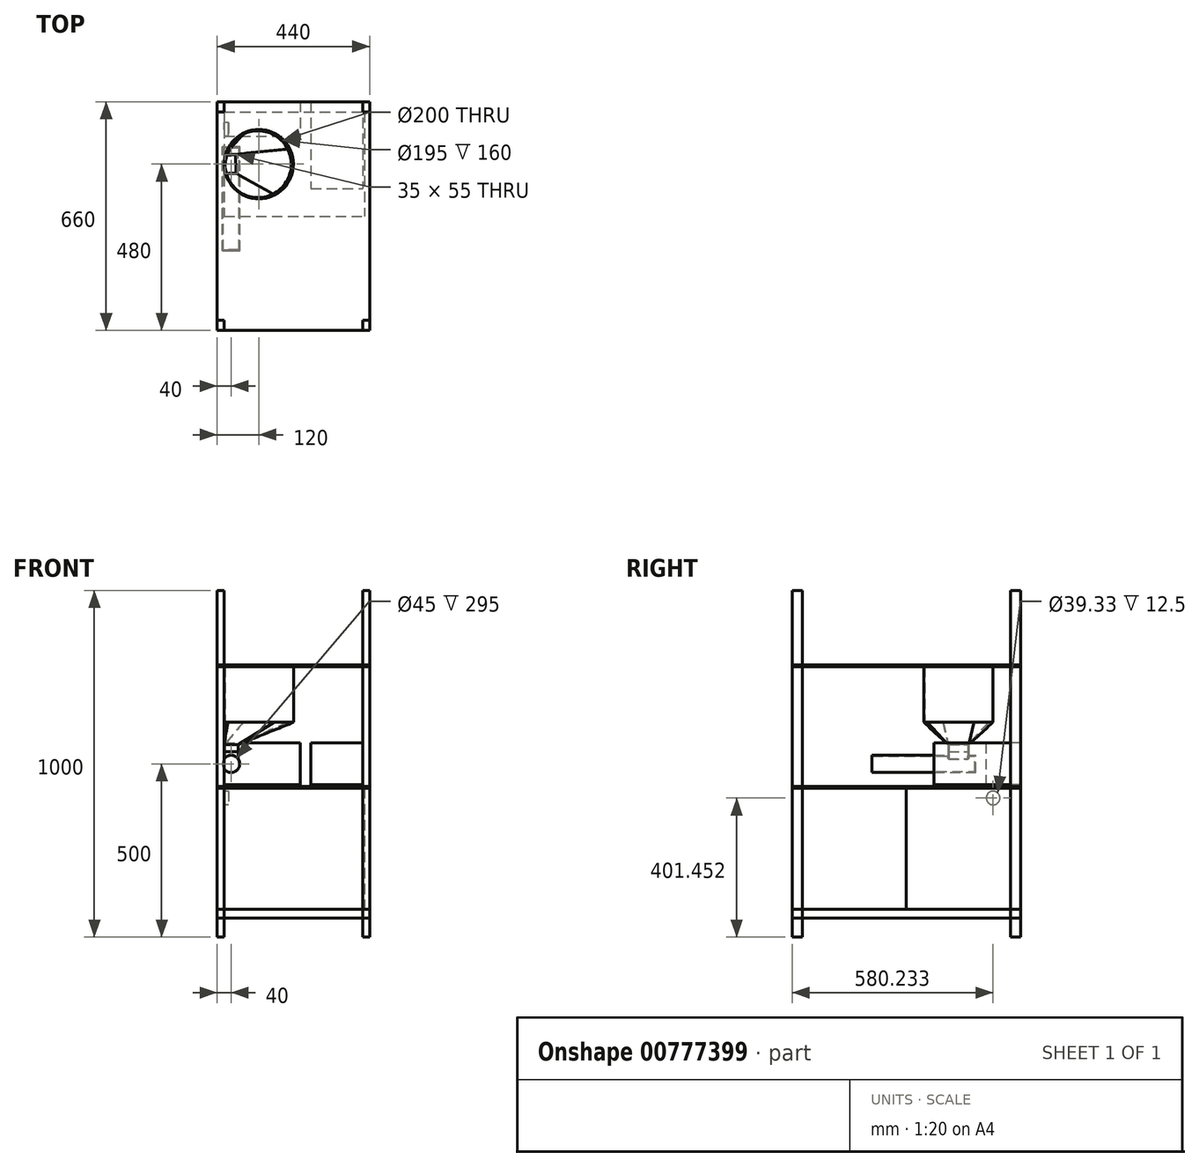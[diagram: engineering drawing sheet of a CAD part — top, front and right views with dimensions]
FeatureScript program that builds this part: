
annotation { "Feature Type Name" : "Feature", "Feature Type Description" : "" }
export const myFeature = defineFeature(function(context is Context, id is Id, definition is map)
    precondition{}
    {
        {
            var Q0;
            Q0=qCreatedBy(makeId("Front.planeOp"),FACE);
            var sketch = newSketch(context, id + "F0", { "sketchPlane" : qUnion([Q0])});
            skCircle(sketch, "E0", {"center": v(0, 0) * mm, "radius": 25 * mm});
            skSolve(sketch);
        }
        {
            var Q0;
            Q0=qSketchRegion(id+"F0",true);
            extrude(context, id + "F1", {"entities" : qUnion([Q0]), "endBound" : BoundingType.SYMMETRIC, "depth" : 300 * mm, "offsetDistance" : 25 * mm});
        }
        {
            var Q0;
            Q0=qCreatedBy(makeId("Top.planeOp"),FACE);
            var sketch = newSketch(context, id + "F2", { "sketchPlane" : qUnion([Q0])});
            skLineSegment(sketch, "E1.bottom", {"start": v(20, 70) * mm, "end": v(-20, 70) * mm});
            skLineSegment(sketch, "E1.top", {"start": v(20, 130) * mm, "end": v(-20, 130) * mm});
            skLineSegment(sketch, "E1.left", {"start": v(20, 70) * mm, "end": v(20, 130) * mm});
            skLineSegment(sketch, "E1.right", {"start": v(-20, 70) * mm, "end": v(-20, 130) * mm});
            skPoint(sketch, "E1.middle", {"position": v(0, 100) * mm});
            skSolve(sketch);
        }
        {
            var Q0;
            Q0=qSketchRegion(id+"F2",true);
            extrude(context, id + "F3", {"entities" : qUnion([Q0]), "operationType" : NewBodyOperationType.ADD, "depth" : 35 * mm, "offsetDistance" : 25 * mm});
        }
        {
            var Q0;
            Q0=makeQuery(id+"F3.opExtrude","CAP_FACE",FACE,{"disambiguationData":[OSD([sQuery(id+"F2.wireOp",EDGE,"E1.bottom"),sQuery(id+"F2.wireOp",EDGE,"E1.top"),sQuery(id+"F2.wireOp",EDGE,"E1.left"),sQuery(id+"F2.wireOp",EDGE,"E1.right")])],"isStart":false});
            shell(context, id + "F4", {"entities" : qUnion([Q0]), "thickness" : 2.5 * mm});
        }
        {
            var Q0;
            Q0=makeQuery(id+"F3.opExtrude","CAP_FACE",FACE,{"disambiguationData":[OSD([sQuery(id+"F2.wireOp",EDGE,"E1.bottom"),sQuery(id+"F2.wireOp",EDGE,"E1.top"),sQuery(id+"F2.wireOp",EDGE,"E1.left"),sQuery(id+"F2.wireOp",EDGE,"E1.right")])],"isStart":false});
            cPlane(context, id + "F5", {"entities" : qUnion([Q0]), "cplaneType" : CPlaneType.OFFSET, "offset" : 0 * mm, "width" : 150 * mm, "height" : 150 * mm});
        }
        {
            var Q0;
            Q0=qCreatedBy(id+"F5.planeOp",FACE);
            var sketch = newSketch(context, id + "F6", { "sketchPlane" : qUnion([Q0])});
            skLineSegment(sketch, "E2.0.0", {"start": v(20, 70) * mm, "end": v(20, 130) * mm});
            skLineSegment(sketch, "E2.0.1", {"start": v(20, 130) * mm, "end": v(-20, 130) * mm});
            skLineSegment(sketch, "E2.0.2", {"start": v(-20, 130) * mm, "end": v(-20, 70) * mm});
            skLineSegment(sketch, "E2.0.3", {"start": v(-20, 70) * mm, "end": v(20, 70) * mm});
            skSolve(sketch);
        }
        {
            var Q0;
            Q0=qSketchRegion(id+"F6",true);
            extrude(context, id + "F7", {"entities" : qUnion([Q0]), "depth" : 20 * mm, "offsetDistance" : 25 * mm});
        }
        {
            var Q0;
            Q0=qCreatedBy(makeId("Top.planeOp"),FACE);
            cPlane(context, id + "F8", {"entities" : qUnion([Q0]), "cplaneType" : CPlaneType.OFFSET, "offset" : 120 * mm, "width" : 150 * mm, "height" : 150 * mm});
        }
        {
            var Q0;
            Q0=qCreatedBy(id+"F8.planeOp",FACE);
            var sketch = newSketch(context, id + "F9", { "sketchPlane" : qUnion([Q0])});
            skPoint(sketch, "E3.middle", {"position": v(80, 100) * mm});
            skLineSegment(sketch, "E4", {"start": v(202.68, 100) * mm, "end": v(-56.4, 100) * mm, "construction": true});
            skPoint(sketch, "E4.startSnap0", {"position": v(180, 100) * mm});
            skCircle(sketch, "E5", {"center": v(80, 100) * mm, "radius": 100 * mm});
            skSolve(sketch);
        }
        {
            var Q0;
            Q0=qSketchRegion(id+"F9",true);
            extrude(context, id + "F10", {"entities" : qUnion([Q0]), "depth" : 160 * mm, "offsetDistance" : 25 * mm});
        }
        {
            var Q0;
            Q0=qCreatedBy(makeId("Top.planeOp"),FACE);
            var sketch = newSketch(context, id + "F11", { "sketchPlane" : qUnion([Q0])});
            skLineSegment(sketch, "E6.bottom", {"start": v(-20, 250) * mm, "end": v(-40, 250) * mm});
            skLineSegment(sketch, "E6.top", {"start": v(-20, 280) * mm, "end": v(-40, 280) * mm});
            skLineSegment(sketch, "E6.left", {"start": v(-20, 250) * mm, "end": v(-20, 280) * mm});
            skLineSegment(sketch, "E6.right", {"start": v(-40, 250) * mm, "end": v(-40, 280) * mm});
            skPoint(sketch, "E6.middle", {"position": v(-30, 265) * mm});
            skLineSegment(sketch, "E7.MirrorCS", {"start": v(380, 250) * mm, "end": v(400, 250) * mm});
            skLineSegment(sketch, "E8.MirrorCS", {"start": v(380, 280) * mm, "end": v(400, 280) * mm});
            skLineSegment(sketch, "E9.MirrorCS", {"start": v(380, 250) * mm, "end": v(380, 280) * mm});
            skLineSegment(sketch, "E10.MirrorCS", {"start": v(400, 250) * mm, "end": v(400, 280) * mm});
            skPoint(sketch, "E11.MirrorP", {"position": v(390, 265) * mm});
            skLineSegment(sketch, "E12.MirrorCS", {"start": v(-20, -380) * mm, "end": v(-40, -380) * mm});
            skLineSegment(sketch, "E13.MirrorCS", {"start": v(-20, -350) * mm, "end": v(-40, -350) * mm});
            skLineSegment(sketch, "E14.MirrorCS", {"start": v(-40, -350) * mm, "end": v(-40, -380) * mm});
            skLineSegment(sketch, "E15.MirrorCS", {"start": v(400, -350) * mm, "end": v(400, -380) * mm});
            skLineSegment(sketch, "E16.MirrorCS", {"start": v(380, -350) * mm, "end": v(380, -380) * mm});
            skLineSegment(sketch, "E17.MirrorCS", {"start": v(380, -380) * mm, "end": v(400, -380) * mm});
            skLineSegment(sketch, "E18.MirrorCS", {"start": v(-20, -350) * mm, "end": v(-20, -380) * mm});
            skLineSegment(sketch, "E19.MirrorCS", {"start": v(380, -350) * mm, "end": v(400, -350) * mm});
            skPoint(sketch, "E20.MirrorP", {"position": v(-30, -365) * mm});
            skPoint(sketch, "E21.MirrorP", {"position": v(390, -365) * mm});
            skSolve(sketch);
        }
        {
            var Q0;
            Q0=qSketchRegion(id+"F11",true);
            extrude(context, id + "F12", {"entities" : qUnion([Q0]), "endBound" : BoundingType.SYMMETRIC, "depth" : 1000 * mm, "offsetDistance" : 25 * mm});
        }
        {
            var Q0;
            Q0=qCreatedBy(makeId("Top.planeOp"),FACE);
            cPlane(context, id + "F13", {"entities" : qUnion([Q0]), "cplaneType" : CPlaneType.OFFSET, "offset" : 70 * mm, "oppositeDirection" : true, "width" : 150 * mm, "height" : 150 * mm});
        }
        {
            var Q0;
            Q0=qCreatedBy(makeId("Top.planeOp"),FACE);
            var sketch = newSketch(context, id + "F14", { "sketchPlane" : qUnion([Q0])});
            skLineSegment(sketch, "E22.bottom", {"start": v(-20, 280) * mm, "end": v(200, 280) * mm});
            skLineSegment(sketch, "E22.top", {"start": v(-20, 180) * mm, "end": v(200, 180) * mm});
            skLineSegment(sketch, "E22.left", {"start": v(-20, 280) * mm, "end": v(-20, 180) * mm});
            skLineSegment(sketch, "E22.right", {"start": v(200, 280) * mm, "end": v(200, 180) * mm});
            skLineSegment(sketch, "E23", {"start": v(0, 86.99) * mm, "end": v(0, 382.57) * mm, "construction": true});
            skSolve(sketch);
        }
        {
            var Q0;
            Q0=qSketchRegion(id+"F14",true);
            extrude(context, id + "F15", {"entities" : qUnion([Q0]), "endBound" : BoundingType.SYMMETRIC, "depth" : 120 * mm, "offsetDistance" : 25 * mm});
        }
        {
            var Q0;
            Q0=qCreatedBy(id+"F13.planeOp",FACE);
            var sketch = newSketch(context, id + "F16", { "sketchPlane" : qUnion([Q0])});
            skLineSegment(sketch, "E24.bottom", {"start": v(-40, 280) * mm, "end": v(400, 280) * mm});
            skLineSegment(sketch, "E24.top", {"start": v(-40, -380) * mm, "end": v(400, -380) * mm});
            skLineSegment(sketch, "E24.left", {"start": v(-40, 280) * mm, "end": v(-40, -380) * mm});
            skLineSegment(sketch, "E24.right", {"start": v(400, 280) * mm, "end": v(400, -380) * mm});
            skPoint(sketch, "E25.0.1.end.orphan", {"position": v(380, -380) * mm});
            skPoint(sketch, "E25.0.0.end.orphan", {"position": v(380, -350) * mm});
            skPoint(sketch, "E25.0.0.start.orphan", {"position": v(400, -350) * mm});
            skPoint(sketch, "E26.0.0.start.orphan", {"position": v(-20, 250) * mm});
            skPoint(sketch, "E26.0.1.start.orphan", {"position": v(-20, 280) * mm});
            skPoint(sketch, "E26.0.2.end.orphan", {"position": v(-40, 250) * mm});
            skSolve(sketch);
        }
        {
            var Q0;
            Q0=qSketchRegion(id+"F16",true);
            extrude(context, id + "F17", {"entities" : qUnion([Q0]), "depth" : 5 * mm, "offsetDistance" : 25 * mm});
        }
        {
            var Q0;
            Q0=qCreatedBy(id+"F13.planeOp",FACE);
            cPlane(context, id + "F18", {"entities" : qUnion([Q0]), "cplaneType" : CPlaneType.OFFSET, "offset" : 350 * mm, "width" : 150 * mm, "height" : 150 * mm});
        }
        {
            var Q0;
            Q0=qCreatedBy(id+"F18.planeOp",FACE);
            var sketch = newSketch(context, id + "F19", { "sketchPlane" : qUnion([Q0])});
            skPoint(sketch, "E27.0", {"position": v(-40, 280) * mm});
            skPoint(sketch, "E28.0", {"position": v(400, -380) * mm});
            skLineSegment(sketch, "E29.bottom", {"start": v(-40, 280) * mm, "end": v(400, 280) * mm});
            skLineSegment(sketch, "E29.top", {"start": v(-40, -380) * mm, "end": v(400, -380) * mm});
            skLineSegment(sketch, "E29.left", {"start": v(-40, 280) * mm, "end": v(-40, -380) * mm});
            skLineSegment(sketch, "E29.right", {"start": v(400, 280) * mm, "end": v(400, -380) * mm});
            skCircle(sketch, "E30.0", {"center": v(80, 100) * mm, "radius": 100 * mm});
            skSolve(sketch);
        }
        {
            var Q0;
            Q0=qSketchRegion(id+"F19",true);
            extrude(context, id + "F20", {"entities" : qUnion([Q0]), "depth" : 5 * mm, "offsetDistance" : 25 * mm});
        }
        {
            var Q0;
            Q0=qCreatedBy(makeId("Top.planeOp"),FACE);
            var sketch = newSketch(context, id + "F21", { "sketchPlane" : qUnion([Q0])});
            skLineSegment(sketch, "E31.bottom", {"start": v(230, 280) * mm, "end": v(380, 280) * mm});
            skLineSegment(sketch, "E31.top", {"start": v(230, 30) * mm, "end": v(380, 30) * mm});
            skLineSegment(sketch, "E31.left", {"start": v(230, 280) * mm, "end": v(230, 30) * mm});
            skLineSegment(sketch, "E31.right", {"start": v(380, 280) * mm, "end": v(380, 30) * mm});
            skPoint(sketch, "E32.0", {"position": v(400, 280) * mm});
            skPoint(sketch, "E33.0", {"position": v(380, 280) * mm});
            skPoint(sketch, "E34.0", {"position": v(380, 250) * mm});
            skPoint(sketch, "E35.0", {"position": v(400, 250) * mm});
            skSolve(sketch);
        }
        {
            var Q0;
            Q0=qSketchRegion(id+"F21",true);
            extrude(context, id + "F22", {"entities" : qUnion([Q0]), "endBound" : BoundingType.SYMMETRIC, "depth" : 120 * mm, "offsetDistance" : 25 * mm});
        }
        {
            var Q0;
            Q0=makeQuery(id+"F17.opExtrude","CAP_FACE",FACE,{"disambiguationData":[OSD([sQuery(id+"F16.wireOp",EDGE,"E24.bottom"),sQuery(id+"F16.wireOp",EDGE,"E24.top"),sQuery(id+"F16.wireOp",EDGE,"E24.left"),sQuery(id+"F16.wireOp",EDGE,"E24.right")])],"isStart":true});
            cPlane(context, id + "F23", {"entities" : qUnion([Q0]), "cplaneType" : CPlaneType.OFFSET, "offset" : 350 * mm, "width" : 150 * mm, "height" : 150 * mm});
        }
        {
            var Q0;
            Q0=qCreatedBy(id+"F23.planeOp",FACE);
            var sketch = newSketch(context, id + "F24", { "sketchPlane" : qUnion([Q0])});
            skPoint(sketch, "E36.0", {"position": v(-40, -280) * mm});
            skPoint(sketch, "E37.0", {"position": v(400, 380) * mm});
            skLineSegment(sketch, "E38.bottom", {"start": v(-40, -280) * mm, "end": v(400, -280) * mm});
            skLineSegment(sketch, "E38.top", {"start": v(-40, 380) * mm, "end": v(400, 380) * mm});
            skLineSegment(sketch, "E38.left", {"start": v(-40, -280) * mm, "end": v(-40, 380) * mm});
            skLineSegment(sketch, "E38.right", {"start": v(400, -280) * mm, "end": v(400, 380) * mm});
            skSolve(sketch);
        }
        {
            var Q0;
            Q0=qSketchRegion(id+"F24",true);
            extrude(context, id + "F25", {"entities" : qUnion([Q0]), "depth" : 25 * mm, "offsetDistance" : 25 * mm});
        }
        {
            var Q0;
            Q0=makeQuery(id+"F10.opExtrude","CAP_FACE",FACE,{"disambiguationData":[OSD([sQuery(id+"F9.wireOp",EDGE,"E5")])],"isStart":true});
            var Q1;
            Q1=makeQuery(id+"F7.opExtrude","CAP_FACE",FACE,{"disambiguationData":[OSD([sQuery(id+"F6.wireOp",EDGE,"E2.0.0"),sQuery(id+"F6.wireOp",EDGE,"E2.0.1"),sQuery(id+"F6.wireOp",EDGE,"E2.0.2"),sQuery(id+"F6.wireOp",EDGE,"E2.0.3")])],"isStart":false});
            loft(context, id + "F26", {"sheetProfilesArray" : [{ "sheetProfileEntities" : qUnion([Q0]) }, { "sheetProfileEntities" : qUnion([Q1]) }]});
        }
        {
            var Q0;
            Q0=makeQuery(id+"F10.opExtrude","CAP_FACE",FACE,{"disambiguationData":[OSD([sQuery(id+"F9.wireOp",EDGE,"E5")])],"isStart":true});
            var Q1;
            Q1=makeQuery(id+"F10.opExtrude","CAP_FACE",FACE,{"disambiguationData":[OSD([sQuery(id+"F9.wireOp",EDGE,"E5")])],"isStart":false});
            var Q2;
            Q2=makeQuery(id+"F7.opExtrude","CAP_FACE",FACE,{"disambiguationData":[OSD([sQuery(id+"F6.wireOp",EDGE,"E2.0.0"),sQuery(id+"F6.wireOp",EDGE,"E2.0.1"),sQuery(id+"F6.wireOp",EDGE,"E2.0.2"),sQuery(id+"F6.wireOp",EDGE,"E2.0.3")])],"isStart":false});
            var Q3;
            Q3=makeQuery(id+"F7.opExtrude","CAP_FACE",FACE,{"disambiguationData":[OSD([sQuery(id+"F6.wireOp",EDGE,"E2.0.0"),sQuery(id+"F6.wireOp",EDGE,"E2.0.1"),sQuery(id+"F6.wireOp",EDGE,"E2.0.2"),sQuery(id+"F6.wireOp",EDGE,"E2.0.3")])],"isStart":true});
            var Q4;
            Q4=makeQuery(id+"F26.opLoft","CAP_FACE",FACE,{"disambiguationData":[OSD([sQuery(id+"F9.wireOp",EDGE,"E5")])],"isStart":true});
            var Q5;
            Q5=makeQuery(id+"F26.opLoft","CAP_FACE",FACE,{"disambiguationData":[OSD([sQuery(id+"F6.wireOp",EDGE,"E2.0.0"),sQuery(id+"F6.wireOp",EDGE,"E2.0.1"),sQuery(id+"F6.wireOp",EDGE,"E2.0.2"),sQuery(id+"F6.wireOp",EDGE,"E2.0.3")])],"isStart":true});
            shell(context, id + "F27", {"entities" : qUnion([Q0, Q1, Q2, Q3, Q4, Q5]), "thickness" : 2.5 * mm});
        }
        {
            var Q0;
            Q0=makeQuery(id+"F25.opExtrude","CAP_FACE",FACE,{"disambiguationData":[OSD([sQuery(id+"F24.wireOp",EDGE,"E38.bottom"),sQuery(id+"F24.wireOp",EDGE,"E38.top"),sQuery(id+"F24.wireOp",EDGE,"E38.left"),sQuery(id+"F24.wireOp",EDGE,"E38.right")])],"isStart":true});
            var sketch = newSketch(context, id + "F28", { "sketchPlane" : qUnion([Q0])});
            skPoint(sketch, "E39.0", {"position": v(-20, 250) * mm});
            skPoint(sketch, "E40.0", {"position": v(380, 250) * mm});
            skLineSegment(sketch, "E41.bottom", {"start": v(-20, 250) * mm, "end": v(385.62, 250) * mm});
            skLineSegment(sketch, "E41.top", {"start": v(-20, -50) * mm, "end": v(385.62, -50) * mm});
            skLineSegment(sketch, "E41.left", {"start": v(-20, 250) * mm, "end": v(-20, -50) * mm});
            skLineSegment(sketch, "E41.right", {"start": v(385.62, 250) * mm, "end": v(385.62, -50) * mm});
            skSolve(sketch);
        }
        {
            var Q0;
            Q0 = qSketchRegion(id + "F28", true);
            extrude(context, id + "F29", {"entities" : qUnion([Q0]), "depth" : 350 * mm, "offsetDistance" : 25 * mm});
        }
        {
            var Q0;
            Q0=makeQuery(id+"F29.opExtrude","SWEPT_FACE",FACE,{"disambiguationData":[OSD([sQuery(id+"F28.wireOp",EDGE,"E41.left")])]});
            var sketch = newSketch(context, id + "F30", { "sketchPlane" : qUnion([Q0])});
            skCircle(sketch, "E42", {"center": v(-200.23, -98.55) * mm, "radius": 19.67 * mm});
            skSolve(sketch);
        }
        {
            var Q0;
            Q0 = qSketchRegion(id + "F30", true);
            extrude(context, id + "F31", {"entities" : qUnion([Q0]), "operationType" : NewBodyOperationType.REMOVE, "endBound" : BoundingType.SYMMETRIC, "oppositeDirection" : true, "depth" : 25 * mm, "offsetDistance" : 25 * mm});
        }
    });
